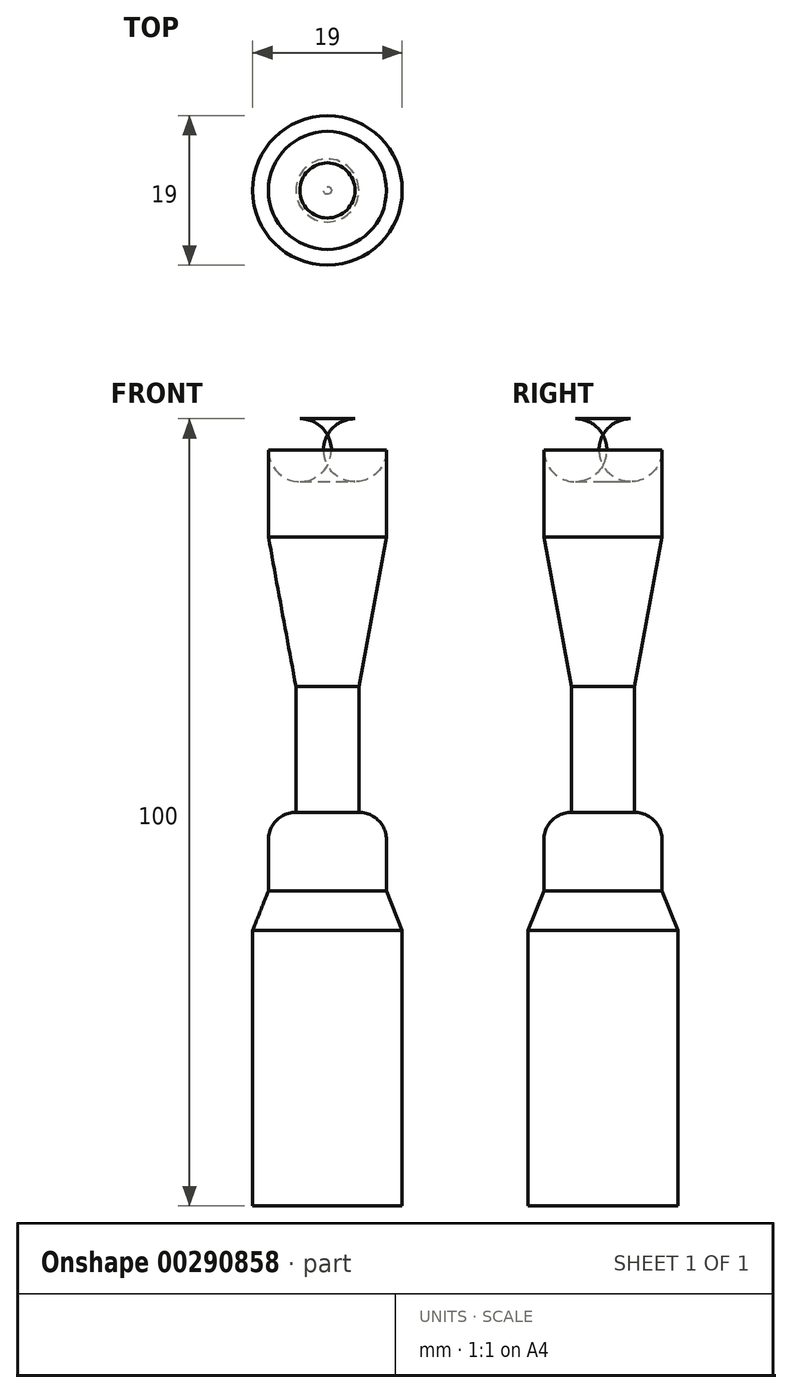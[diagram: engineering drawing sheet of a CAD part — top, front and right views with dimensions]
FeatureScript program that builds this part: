
annotation { "Feature Type Name" : "Feature", "Feature Type Description" : "" }
export const myFeature = defineFeature(function(context is Context, id is Id, definition is map)
    precondition{}
    {
        {
            var Q0;
            Q0=qCreatedBy(makeId("Front.planeOp"),FACE);
            var sketch = newSketch(context, id + "F0", { "sketchPlane" : qUnion([Q0])});
            skLineSegment(sketch, "E0", {"start": v(3.5, 0) * mm, "end": v(0, 0) * mm});
            skArc(sketch, "E1", {"start": v(7.5, -4) * mm, "mid": v(6.33, -1.17) * mm, "end": v(3.5, 0) * mm});
            skLineSegment(sketch, "E2", {"start": v(7.5, -15) * mm, "end": v(7.5, -4) * mm});
            skLineSegment(sketch, "E3", {"start": v(7.5, -15) * mm, "end": v(4, -34) * mm});
            skLineSegment(sketch, "E4", {"start": v(4, -34) * mm, "end": v(4, -50) * mm});
            skArc(sketch, "E5", {"start": v(7.5, -53.5) * mm, "mid": v(6.47, -51.03) * mm, "end": v(4, -50) * mm});
            skLineSegment(sketch, "E6", {"start": v(7.5, -53.5) * mm, "end": v(7.5, -60) * mm});
            skLineSegment(sketch, "E7", {"start": v(7.5, -60) * mm, "end": v(9.5, -65) * mm});
            skLineSegment(sketch, "E8", {"start": v(9.5, -65) * mm, "end": v(9.5, -100) * mm});
            skLineSegment(sketch, "E9", {"start": v(9.5, -100) * mm, "end": v(0, -100) * mm});
            skLineSegment(sketch, "E10", {"start": v(0, -100) * mm, "end": v(0, 0) * mm});
            skSolve(sketch);
        }
        {
            var Q0;
            Q0=makeQuery(id+"F0.imprint","IMPRINT",FACE,{"disambiguationData":[TD([[makeQuery(id+"F0.imprint","IMPRINT",EDGE,{"derivedFrom":sQuery(id+"F0.wireOp",EDGE,"E0")}),1.0]])]});
            var Q1;
            Q1=sQuery(id+"F0.wireOp",EDGE,"E10");
            revolve(context, id + "F1", {"entities" : qUnion([Q0]), "axis" : qUnion([Q1]), "revolveType" : RevolveType.FULL});
        }
    });
